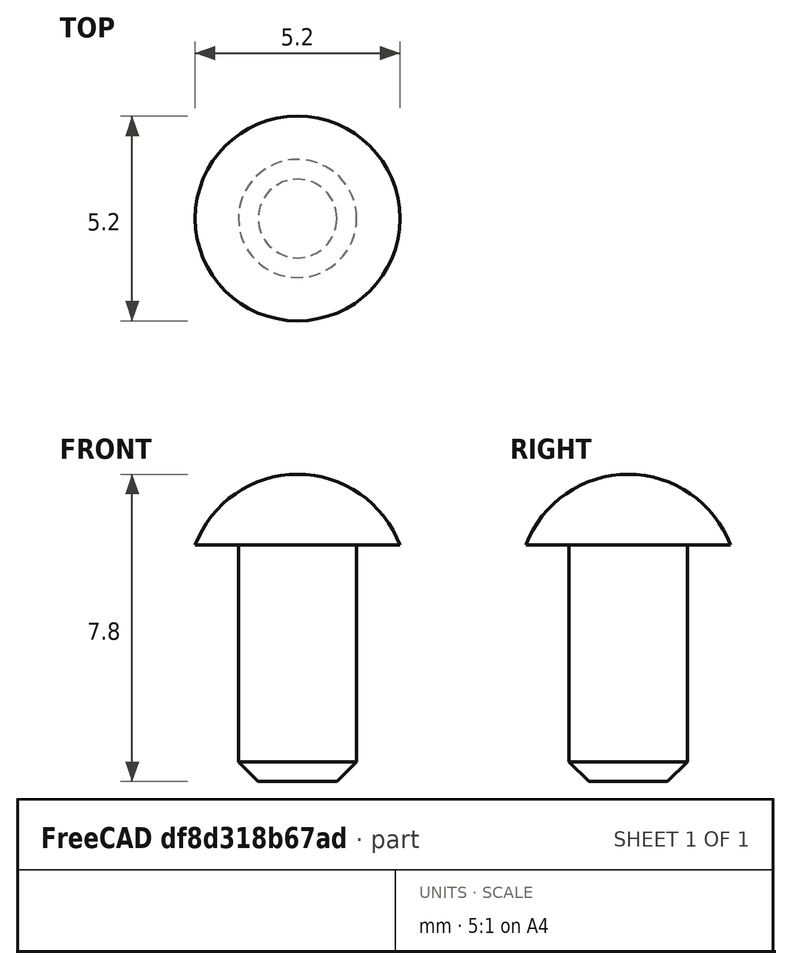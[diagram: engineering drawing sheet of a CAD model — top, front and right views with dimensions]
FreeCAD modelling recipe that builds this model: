
FCSTD DOCUMENT  (FreeCAD 0.14R3700 (Git))
Label: Halbrundkerbnagel-DIN_1476
License: CC-BY 3.0
LicenseURL: http://creativecommons.org/licenses/by/3.0/
objects: Sketcher::SketchObject×1, PartDesign::Revolution×1, Part::Feature×1
note: 4 computed .brp shape members not serialized (recipe doc carries the construction recipe); baked Part::Feature solids carry a one-line shape summary decoded from their .brp

FEATURE [Sketcher::SketchObject] Sketch
  Placement = pos=(0,0,0) rot=(0.57735,0.57735,0.57735;2.0944rad)
  sketch-geometry (6):
    g0: LineSegment StartX=0 StartY=7.8 StartZ=0 EndX=0 EndY=0 EndZ=0
    g1: LineSegment StartX=0 StartY=0 StartZ=0 EndX=1 EndY=0 EndZ=0
    g2: LineSegment StartX=1 StartY=0 StartZ=0 EndX=1.5 EndY=0.5 EndZ=0
    g3: LineSegment StartX=1.5 StartY=0.5 StartZ=0 EndX=1.5 EndY=6 EndZ=0
    g4: LineSegment StartX=1.5 StartY=6 StartZ=0 EndX=2.6 EndY=6 EndZ=0
    g5: ArcOfCircle CenterX=0 CenterY=5.02222 CenterZ=0 NormalX=0 NormalY=0 NormalZ=1 Radius=2.77778 StartAngle=0.359707 EndAngle=1.5708
  constraints (19):
    c: PointOnObject(g0,g-2)
    c: Coincident(g0,g-1)
    c: Coincident(g0,g1)
    c: Horizontal(g1)
    c: Coincident(g1,g2)
    c: Coincident(g2,g3)
    c: Vertical(g3)
    c: Coincident(g3,g4)
    c: Horizontal(g4)
    c: PointOnObject(g5,g0)
    c: Coincident(g5,g4)
    c: PointOnObject(g5,g-2)
    c: Coincident(g0,g5)
    c: DistanceX(g2) = 0.5
    c: DistanceY(g2) = 0.5
    c: DistanceX(g-1,g2) = 1.5
    c: DistanceY(g4,g1) = -6
    c: DistanceX(g4,g0) = -2.6
    c: DistanceY(g4,g0) = 1.8
FEATURE [PartDesign::Revolution] Revolution
  Angle = 360
  Axis = (0,0,1)
  Base = (0,0,0)
  Placement = pos=(0,0,0) rot=(0.57735,0.57735,0.57735;2.0944rad)
  ReferenceAxis = -> Sketch [V_Axis]
  Reversed = true
  Sketch = -> Sketch
FEATURE [Part::Feature] Revolution001  label="Halbrundkerbnagel DIN1476 - 3x6"
  Placement = pos=(0,0,0) rot=(0.57735,0.57735,0.57735;2.0944rad)
  shape: bbox 5.2 x 5.2 x 7.8 mm, 5 faces (baked)
